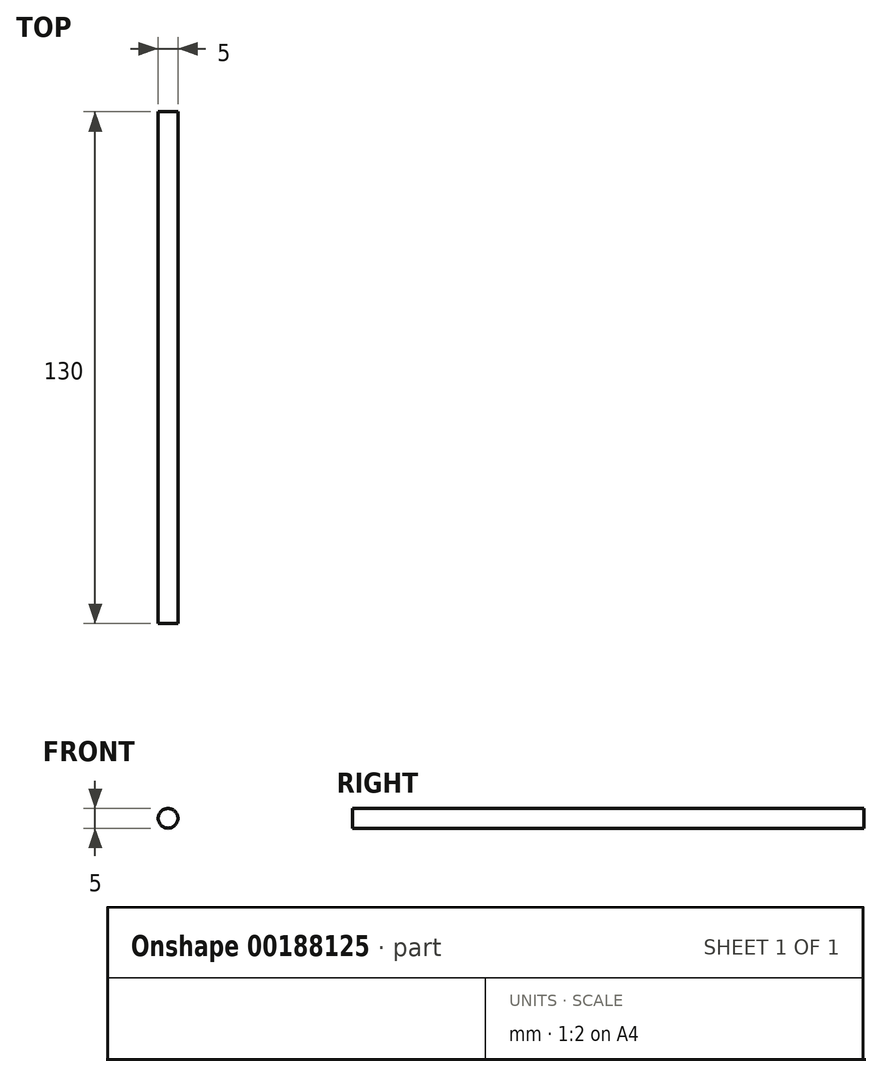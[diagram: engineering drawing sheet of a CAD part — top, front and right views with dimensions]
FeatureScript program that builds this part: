
annotation { "Feature Type Name" : "Feature", "Feature Type Description" : "" }
export const myFeature = defineFeature(function(context is Context, id is Id, definition is map)
    precondition{}
    {
        {
            var Q0;
            Q0=qCreatedBy(makeId("Front.planeOp"),FACE);
            var sketch = newSketch(context, id + "F1", { "sketchPlane" : qUnion([Q0])});
            skCircle(sketch, "E0", {"center": v(0, 0) * mm, "radius": 2.5 * mm});
            skSolve(sketch);
        }
        {
            var Q0;
            Q0 = qSketchRegion(id + "F1", true);
            extrude(context, id + "F0", {"entities" : qUnion([Q0]), "depth" : 130 * mm});
        }
    });
